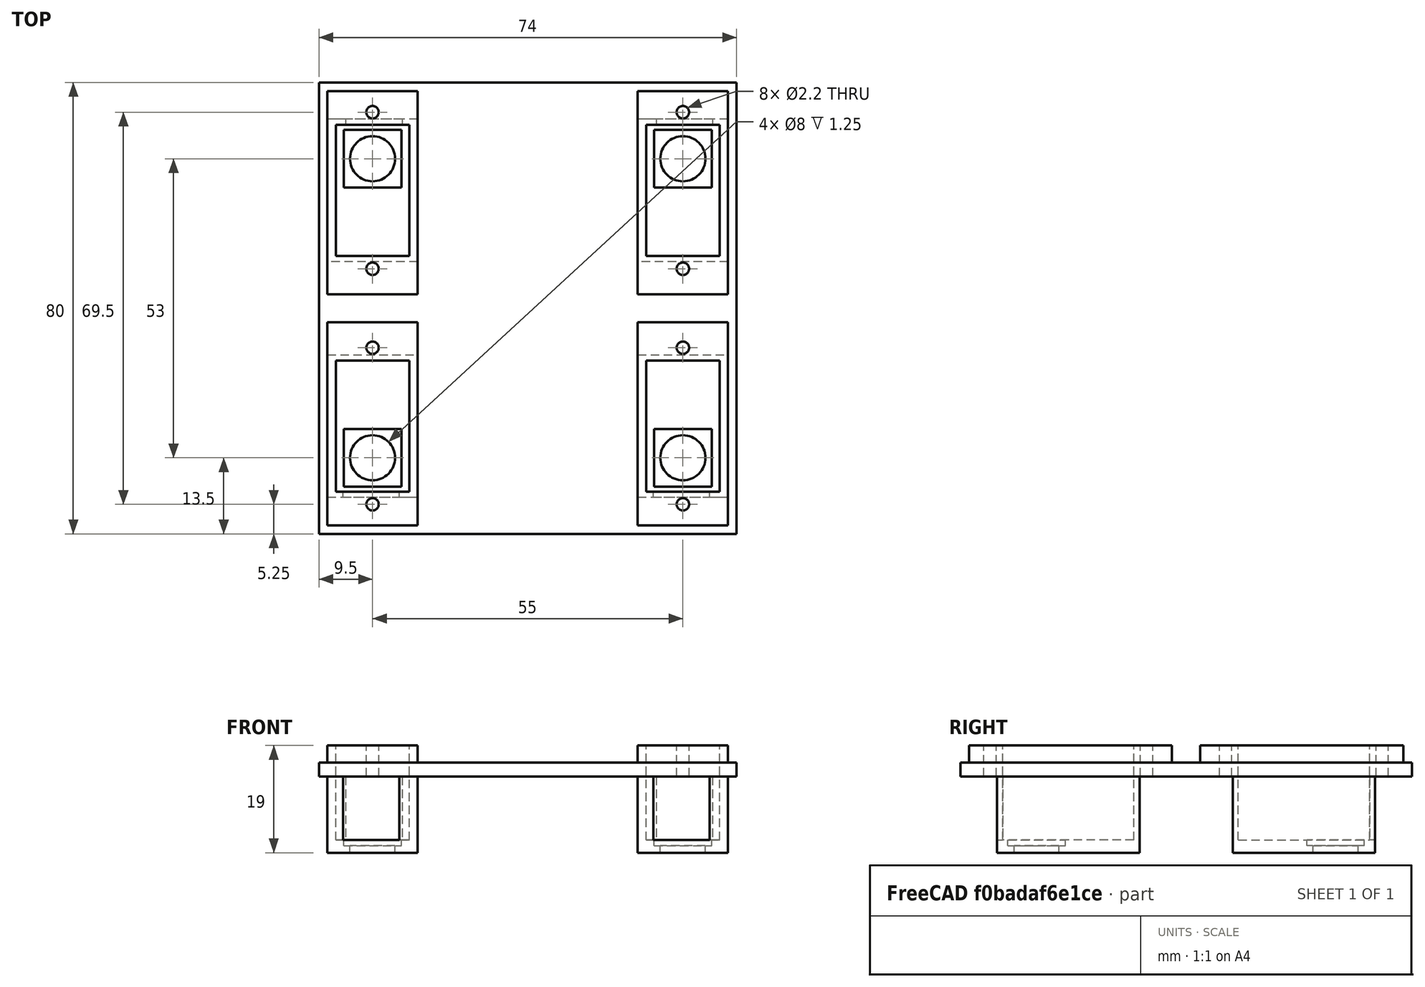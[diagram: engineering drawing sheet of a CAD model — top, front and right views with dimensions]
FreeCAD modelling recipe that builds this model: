
FCSTD DOCUMENT  (FreeCAD 0.18R4 (GitTag))
Label: base
License: All rights reserved
LicenseURL: http://en.wikipedia.org/wiki/All_rights_reserved
objects: Part::Feature×6, Part::FeaturePython×3, Part::Cut×3, Part::Box×2, Part::Offset×1, Part::MultiFuse×1
note: 16 computed .brp shape members not serialized (recipe doc carries the construction recipe); baked Part::Feature solids carry a one-line shape summary decoded from their .brp

FEATURE [Part::Box] Box  label="soporte"
  AttacherType = Attacher::AttachEngine3D
  Height = 2.5
  Length = 74
  Placement = pos=(0,0,8.5) rot=(0,0,1;0rad)
  Width = 80
FEATURE [Part::Box] Box001  label="Cubo001"
  AttacherType = Attacher::AttachEngine3D
  Height = 10
  Length = 12.5
  Placement = pos=(0,4.75,0) rot=(0,0,1;0rad)
  Width = 22.75
FEATURE [Part::Offset] Offset  label="Offset servo"
  Fill = false
  Intersection = false
  Join = 2
  Mode = 0
  Placement = pos=(3.25,3,5) rot=(0,0,1;0rad)
  SelfIntersection = false
  Source = -> Box001
  Value = 0.25
FEATURE [Part::Feature] Part__Feature004  label="SG90_servo_con_tornillos"
  Placement = pos=(3.25,3,0) rot=(0,0,1;0rad)
  shape: bbox 12.5 x 32.25 x 30.45 mm, 42 faces (baked)
FEATURE [Part::FeaturePython] Array  label="mitad servos"  # Draft array (typed FeaturePython)
  Angle = 360
  ArrayType = 0
  Axis = (0,0,1)
  Base = -> Part__Feature004
  Center = (0,0,0)
  Fuse = false
  IntervalAxis = (0,0,0)
  IntervalX = (55,0,0)
  IntervalY = (0,48,0)
  IntervalZ = (0,0,1)
  NumberPolar = 1
  NumberX = 2
  NumberY = 1
  NumberZ = 1
FEATURE [Part::Feature] Part__Feature  label="soporte_motor_con_hueco_tapon"
  Placement = pos=(1.25,2,0) rot=(0,0,1;0rad)
  shape: bbox 16 x 36 x 19 mm, 25 faces (baked)
FEATURE [Part::Feature] Part__Feature006  label="soporte_motor_con_hueco_tapon001"
  Placement = pos=(17.75,78,0) rot=(0,0,1;3.14159rad)
  shape: bbox 16 x 36 x 19 mm, 25 faces (baked)
FEATURE [Part::Feature] Part__Feature007  label="soporte_motor_con_hueco_tapon002"
  Placement = pos=(72.75,78,0) rot=(0,0,1;3.14159rad)
  shape: bbox 16 x 36 x 19 mm, 25 faces (baked)
FEATURE [Part::Feature] Part__Feature008  label="soporte_motor_con_hueco_tapon003"
  Placement = pos=(56.25,2,0) rot=(0,0,1;0rad)
  shape: bbox 16 x 36 x 19 mm, 25 faces (baked)
FEATURE [Part::Feature] Part__Feature009  label="SG90_servo_con_tornillos002"
  Placement = pos=(3.25,3,0) rot=(0,0,1;0rad)
  shape: bbox 12.5 x 32.25 x 30.45 mm, 42 faces (baked)
FEATURE [Part::FeaturePython] Array001  label="mitad servos001"  # Draft array (typed FeaturePython)
  Angle = 360
  ArrayType = 0
  Axis = (0,0,1)
  Base = -> Part__Feature009
  Center = (0,0,0)
  Fuse = false
  IntervalAxis = (0,0,0)
  IntervalX = (55,0,0)
  IntervalY = (0,48,0)
  IntervalZ = (0,0,1)
  NumberPolar = 1
  NumberX = 2
  NumberY = 1
  NumberZ = 1
  Placement = pos=(0,41.75,0) rot=(0,0,1;0rad)
FEATURE [Part::Cut] Cut
  Base = -> Box
  Refine = true
  Tool = -> Array
FEATURE [Part::Cut] Cut001  label="soporte perforado"
  Base = -> Cut
  Refine = true
  Tool = -> Array001
FEATURE [Part::FeaturePython] Array002  # Draft array (typed FeaturePython)
  Angle = 360
  ArrayType = 0
  Axis = (0,0,1)
  Base = -> Offset
  Center = (0,0,0)
  Fuse = false
  IntervalAxis = (0,0,0)
  IntervalX = (55,0,0)
  IntervalY = (0,41.75,0)
  IntervalZ = (0,0,1)
  NumberPolar = 1
  NumberX = 2
  NumberY = 2
  NumberZ = 1
FEATURE [Part::Cut] Cut002  label="soporte perforado offset"
  Base = -> Cut001
  Placement = pos=(0,0,2.5) rot=(0,0,1;0rad)
  Refine = true
  Tool = -> Array002
FEATURE [Part::MultiFuse] Fusion  label="base"
  Refine = true
  Shapes = -> [Cut002,Part__Feature,Part__Feature006,Part__Feature007,Part__Feature008]
